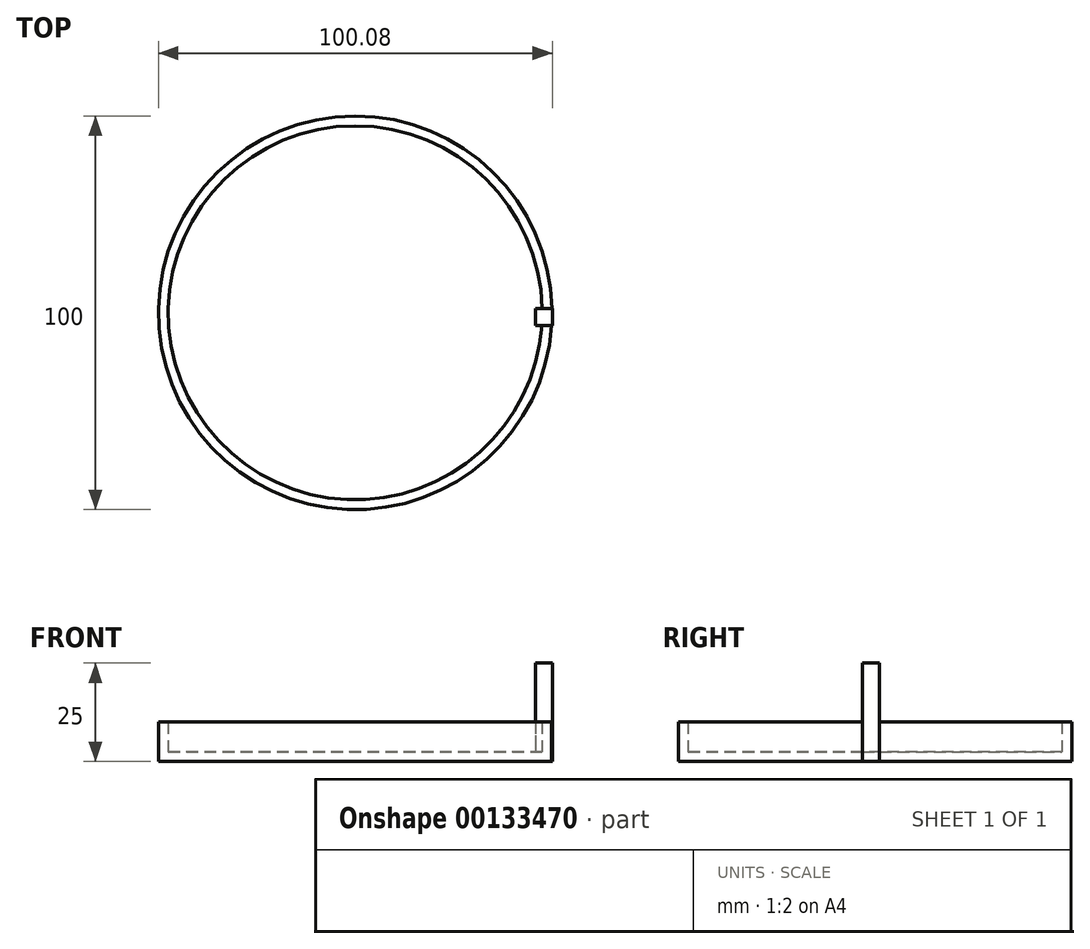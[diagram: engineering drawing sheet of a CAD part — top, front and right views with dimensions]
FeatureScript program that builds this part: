
annotation { "Feature Type Name" : "Feature", "Feature Type Description" : "" }
export const myFeature = defineFeature(function(context is Context, id is Id, definition is map)
    precondition{}
    {
        {
            var Q0;
            Q0=qCreatedBy(makeId("Top.planeOp"),FACE);
            var sketch = newSketch(context, id + "F0", { "sketchPlane" : qUnion([Q0])});
            skCircle(sketch, "E0", {"center": v(-0.8, 0.34) * mm, "radius": 50 * mm});
            skSolve(sketch);
        }
        {
            var Q0;
            Q0=makeQuery(id+"F0.imprint","IMPRINT",FACE,{"disambiguationData":[TD([[makeQuery(id+"F0.imprint","IMPRINT",EDGE,{"derivedFrom":sQuery(id+"F0.wireOp",EDGE,"E0")}),1.0]])]});
            extrude(context, id + "F1", {"entities" : qUnion([Q0]), "depth" : 10 * mm});
        }
        {
            var Q0;
            Q0=makeQuery(id+"F1.opExtrude","CAP_FACE",FACE,{"disambiguationData":[OSD([sQuery(id+"F0.wireOp",EDGE,"E0")])],"isStart":false});
            shell(context, id + "F2", {"entities" : qUnion([Q0]), "thickness" : 2.5 * mm});
        }
        {
            var Q0;
            Q0=qCreatedBy(makeId("Top.planeOp"),FACE);
            var sketch = newSketch(context, id + "F3", { "sketchPlane" : qUnion([Q0])});
            skLineSegment(sketch, "E1.bottom", {"start": v(49.28, 1.47) * mm, "end": v(44.98, 1.47) * mm});
            skLineSegment(sketch, "E1.top", {"start": v(49.28, -2.83) * mm, "end": v(44.98, -2.83) * mm});
            skLineSegment(sketch, "E1.left", {"start": v(49.28, 1.47) * mm, "end": v(49.28, -2.83) * mm});
            skLineSegment(sketch, "E1.right", {"start": v(44.98, 1.47) * mm, "end": v(44.98, -2.83) * mm});
            skSolve(sketch);
        }
        {
            var Q0;
            Q0=makeQuery(id+"F3.imprint","IMPRINT",FACE,{"disambiguationData":[TD([[makeQuery(id+"F3.imprint","IMPRINT",EDGE,{"derivedFrom":sQuery(id+"F3.wireOp",EDGE,"E1.bottom")}),1.0]])]});
            extrude(context, id + "F4", {"entities" : qUnion([Q0]), "operationType" : NewBodyOperationType.ADD, "depth" : 25 * mm});
        }
    });
